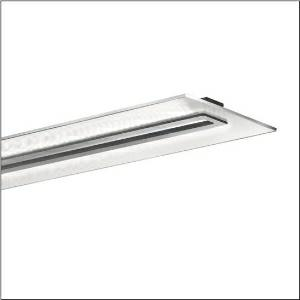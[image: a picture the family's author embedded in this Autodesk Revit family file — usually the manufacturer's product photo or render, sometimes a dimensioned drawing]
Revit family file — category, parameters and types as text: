
# Revit family: vega_r__11_5mn238dle0s_e1af
name_source: partatom
category: Lighting Fixtures
units: mm (PartAtom-declared; Revit-internal decimal feet)

## family parameters
Cut with Voids When Loaded = No
Host = Face
Light Source = No
Part Type = Normal
Room Calculation Point = No
Round Connector Dimension = Use Diameter
Shared = No

## types (1)
- --- (1 x LED 4000K / CRI = 80 (unbekannt), 8130 lm, 4000K)
    Apparent Load = 62 VA
    CIE Flux Codes = 61 86 97 62 100
    Color Rendering = 80
    Color Temperature = 4000K
    Default Elevation = 1800 mm
    Description = Vega® 11, office luminaire, primary light control with prismatic reflector, of PMMA, transparent prismatic structure, CAT 2 (L<= 1500cd/m²), light emission: direct/indirect distribution, primary light characteristic: symmetric, installation type: suspended mounting, surface-mounted, LED, rated luminous flux: 8.130lm, luminous efficacy: 131lm/W, light colour: 840, colour temperature: 4000K, control gear: DALI, with terminal, 3+2-pole, max. 2.5mm², mains connection: 230V, AC, 50Hz, connection cable inclusive, cable length: 1,5m, rated input power: 62W, luminaire housing, rectangular, rounded, of aluminium section, anodised, metallic grey (RAL 9006), length: 1.250mm, width: 350mm, height: 43mm, luminaire housing, lower part, of aluminium section, anodised, metallic grey (RAL 9006), of PC, grey, protection rating (complete): IP20, insulation class (complete): insulation class I (protective earthing), certification: CE, permissible operating ambient temperature: 0..+35°C, standard: EN 50419, packaging unit: 1 piece
    Height = 40 mm  [stored 0.131234 ft]
    Lamp = 1 x LED 4000K / CRI >= 80 (unbekannt)
    Lamp Light Flux = 8130 lm
    Lamp count = 1
    Length = 1250 mm
    Luminous efficacy = 131 lm/W
    Manufacturer = Siteco
    ModVariant = No
    Model = 5MN238DLE0S
    Mounting Place = Ceiling
    Mounting Type = Pendant
    Number of Poles = 1
    OnlyDefault = Yes
    Power Factor = 1
    Product Name = Vega® 11
    Product group = office luminaire | ceiling pendant
    ProductGroupID = 904
    Protection Class = Protection class I
    Protection Degree = IP 20
    RLX_Detail_Level = 1
    RLX_Emergency_Light_Flux = 0 lm
    RLX_Emergency_Type = 0
    RLX_Emergency_Type_DB = No
    RlxData = <blob elided: 62933 chars, md5=ecafb574>
    Socket = socket
    Standby Power = 0 W
    System Light Flux = 8130 lm
    System Power = 62 W
    Type Comments = factory setting: luminous flux: 100 % | dim-lin: 254 | 458 mA
    Type Image = l_1004807.jpg
    URL = http://relux.com
    VarID = @adj_203972
    Voltage = 0 V
    Weight = 0.00 kg
    Width = 350 mm

note: [stored X ft] marks values corroborated as IEEE doubles in the binary element streams (Revit-internal decimal feet)

## geometry (parser evidence)
native form markers: Blend x4, Sweep x11
no freeform markers — native parametric forms only
